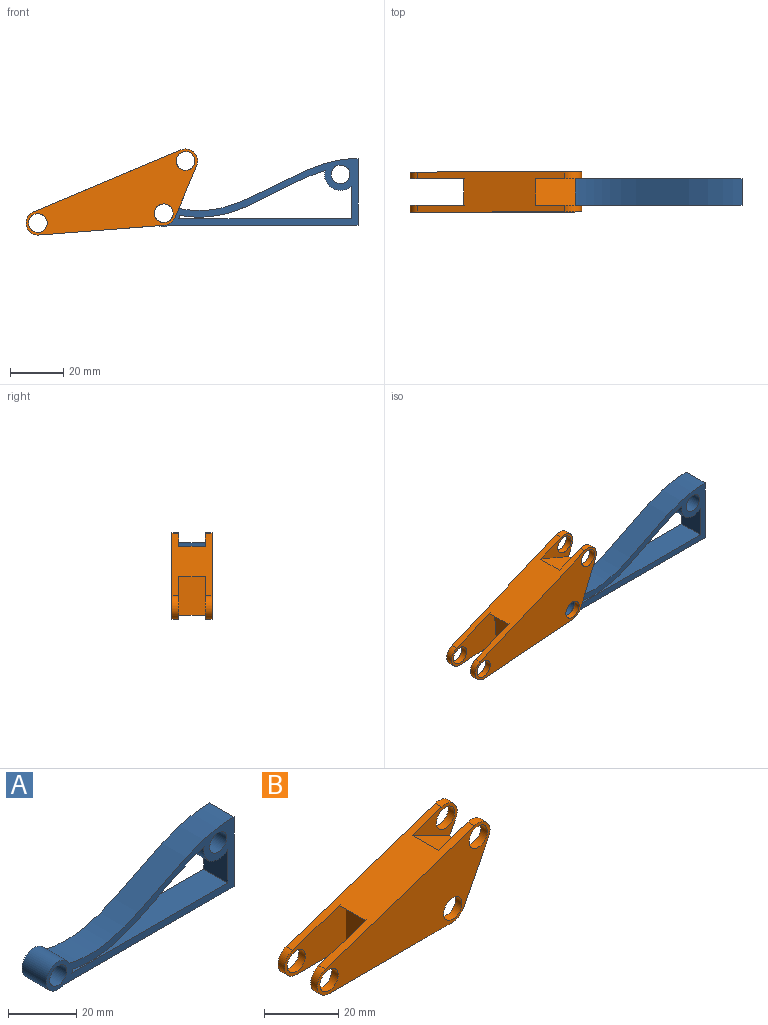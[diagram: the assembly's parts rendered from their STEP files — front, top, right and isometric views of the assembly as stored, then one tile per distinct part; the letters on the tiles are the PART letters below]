
ASSEMBLY  parts=2 mates=1
PART A: 13 faces, bbox 77.8x10x25.5 mm
  f0: plane 77.77x25.52mm, normal (0,-1,0), area 481.7mm2, adj f2,f3,f4,f5,f6,f7,f8,f9
  f1: plane 77.77x25.52mm, normal (0,1,0), area 481.7mm2, adj f2,f3,f4,f5,f6,f7,f8,f9
  f2: cylinder r=5mm len=10mm, axis (0,1,0), area 236.6mm2, adj f0,f1,f3,f6
  f3: plane 70.54x10mm, normal (0,0,-1), area 705.4mm2, adj f0,f1,f2,f4
  f4: plane 25x10mm, normal (1,0,0), area 250mm2, adj f0,f1,f3,f6
  f5: cylinder r=3.5mm len=10mm, axis (0,1,0), area 219.9mm2, adj f0,f1
  f6: extruded ~68.25x19.5mm, area 721.3mm2, adj f0,f1,f2,f4
  f7: cylinder r=3.5mm len=10mm, axis (0,1,0), area 219.9mm2, adj f0,f1
  f8: plane 64.61x10mm, normal (0,0,1), area 646.1mm2, adj f0,f1,f9,f12
  f9: plane 12.13x10mm, normal (-1,0,0), area 121.3mm2, adj f0,f1,f8,f10
  f10: cylinder r=6mm len=10.05mm, axis (0,1,0), area 154mm2, adj f0,f1,f9,f11
  f11: extruded ~54.47x17.57mm, area 581.1mm2, adj f0,f1,f10,f12
  f12: cylinder r=6mm len=10mm, axis (0,1,0), area 12.6mm2, adj f0,f1,f8,f11
PART B: 29 faces, bbox 65.9x15x27.9 mm
  f0: plane 56.94x18.91mm, normal (-0.32,0,0.95), area 593.5mm2, adj f2,f3,f7,f12,f13,f14,f20,f21
  f1: cylinder r=3.5mm len=7mm, axis (0,1,0), area 55mm2, adj f14,f24
  f2: cylinder r=4.5mm len=6.55mm, axis (0,1,0), area 26.6mm2, adj f0,f6,f14,f24
  f3: cylinder r=4.5mm len=8.77mm, axis (0,1,0), area 31.7mm2, adj f0,f8,f13,f22
  f4: cylinder r=3.5mm len=7mm, axis (0,1,0), area 55mm2, adj f13,f22
  f5: cylinder r=3.5mm len=7mm, axis (0,1,0), area 55mm2, adj f14,f15
  f6: plane 18.64x15mm, normal (0.89,0,-0.46), area 191.7mm2, adj f2,f12,f13,f14,f15,f16,f17,f24
  f7: cylinder r=4.5mm len=8.77mm, axis (0,1,0), area 31.7mm2, adj f0,f8,f14,f20
  f8: plane 46.94x15mm, normal (0,0,-1), area 445mm2, adj f3,f7,f13,f14,f15,f17,f18,f20
  f9: cylinder r=3.5mm len=7mm, axis (0,1,0), area 55mm2, adj f14,f20
  f10: cylinder r=3.5mm len=7mm, axis (0,1,0), area 55mm2, adj f13,f25
  f11: cylinder r=3.5mm len=7mm, axis (0,1,0), area 55mm2, adj f13,f17
  f12: cylinder r=4.5mm len=6.55mm, axis (0,1,0), area 26.6mm2, adj f0,f6,f13,f25
  f13: plane 65.94x27.91mm, normal (0,-1,0), area 972.9mm2, adj f0,f3,f4,f6,f8,f10,f11,f12
  f14: plane 65.94x27.91mm, normal (0,1,0), area 972.9mm2, adj f0,f1,f2,f5,f6,f7,f8,f9
  f15: plane 14.56x13.46mm, normal (0,-1,0), area 104.3mm2, adj f5,f6,f8,f16,f18,f19,f27
  f16: plane 10x8.9mm, normal (-0.46,0,-0.89), area 100mm2, adj f6,f15,f17,f19
  f17: plane 14.56x13.46mm, normal (0,1,0), area 104.3mm2, adj f6,f8,f11,f16,f18,f19,f28
  f18: plane 10x10mm, normal (1,0,0), area 100mm2, adj f8,f15,f17,f19
  f19: cylinder r=19.19mm len=10mm, axis (0,1,0), area 66.7mm2, adj f15,f16,f17,f18
  f20: plane 23.48x14.69mm, normal (0,-1,0), area 227.5mm2, adj f0,f7,f8,f9,f21,f23
  f21: plane 10x2.56mm, normal (0,0,-1), area 25.6mm2, adj f0,f20,f22,f23
  f22: plane 23.48x14.69mm, normal (0,1,0), area 227.5mm2, adj f0,f3,f4,f8,f21,f23
  f23: plane 14.69x10mm, normal (-1,0,0), area 146.9mm2, adj f8,f20,f21,f22
  f24: plane 17.17x11.27mm, normal (0,-1,0), area 66.6mm2, adj f0,f1,f2,f6,f26
  f25: plane 17.17x11.27mm, normal (0,1,0), area 66.6mm2, adj f0,f6,f10,f12,f26
  f26: plane 14.26x10mm, normal (0.46,0,0.89), area 160.2mm2, adj f0,f6,f24,f25
  f27: cylinder r=5mm len=4.45mm, axis (0,1,0), area 13.7mm2, adj f6,f8,f14,f15
  f28: cylinder r=5mm len=4.45mm, axis (0,1,0), area 13.7mm2, adj f6,f8,f13,f17
PLACE A t=(3.29,2.03,16.86)mm fixed
PLACE B rot(axis=(0,-1,0),4.4deg) t=(-49.34,-2.97,-10.93)mm
MATE revolute B.f5 <-> A.f2  axis (0,1,0) through (-13.92,-7.97,-3.67)mm
